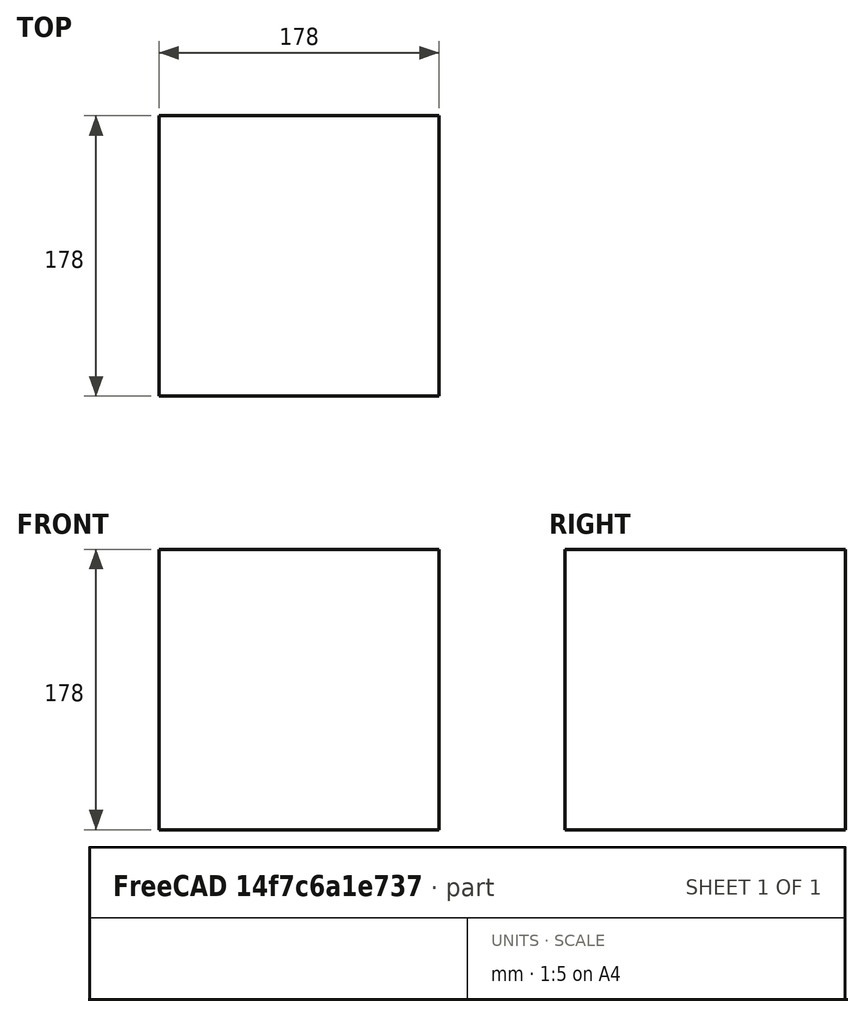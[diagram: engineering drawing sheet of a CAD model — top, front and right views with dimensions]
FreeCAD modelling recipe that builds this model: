
FCSTD DOCUMENT  (FreeCAD 0.20R29177 +426 (Git))
Label: glascube
License: All rights reserved
LicenseURL: http://en.wikipedia.org/wiki/All_rights_reserved
objects: App::FeaturePython×4, Part::Box×1, Mesh::Feature×1, Part::Cut×1
note: 2 computed .brp shape members not serialized (recipe doc carries the construction recipe); baked Part::Feature solids carry a one-line shape summary decoded from their .brp

FEATURE [Part::Box] Box
  AttacherType = Attacher::AttachEngine3D
  Height = 178
  Length = 178
  Width = 178
FEATURE [App::FeaturePython] xy  # WARN: FeaturePython — macro-defined, semantics opaque (R4)
  BaseHeight = 0.5
  LayerHeight = 0.1
  MaximumHeight = 3
  NozzleSize = 0.4
  Path = <userpath>/Documents/glas/glas/glascube/xy.png
  UpdateNotifier = 1
  ppi = 57.7273
FEATURE [App::FeaturePython] glasford_io_big  # WARN: FeaturePython — macro-defined, semantics opaque (R4)
  BaseHeight = 0.5
  LayerHeight = 0.1
  MaximumHeight = 3
  NozzleSize = 0.4
  Path = <userpath>/Documents/glas/glas/glascube/glasford.io_big.png
  UpdateNotifier = 0
  ppi = 300
FEATURE [Mesh::Feature] glasford_io_big_Result
FEATURE [App::FeaturePython] Box_Subtractive  # WARN: FeaturePython — macro-defined, semantics opaque (R4)
  Base = -> Box
  Enabled = true
  Mode = 1
FEATURE [App::FeaturePython] glasford_io_big_Mesh  # WARN: FeaturePython — macro-defined, semantics opaque (R4)
  Features = -> [Box_Subtractive]
  LithophaneImage = -> glasford_io_big
  Result = -> glasford_io_big_Result
FEATURE [Part::Cut] Cut
  Base = -> Box
  Placement = pos=(92,0,0) rot=(0,0,1;0rad)
  Tool = -> glasford_io_big_Result
